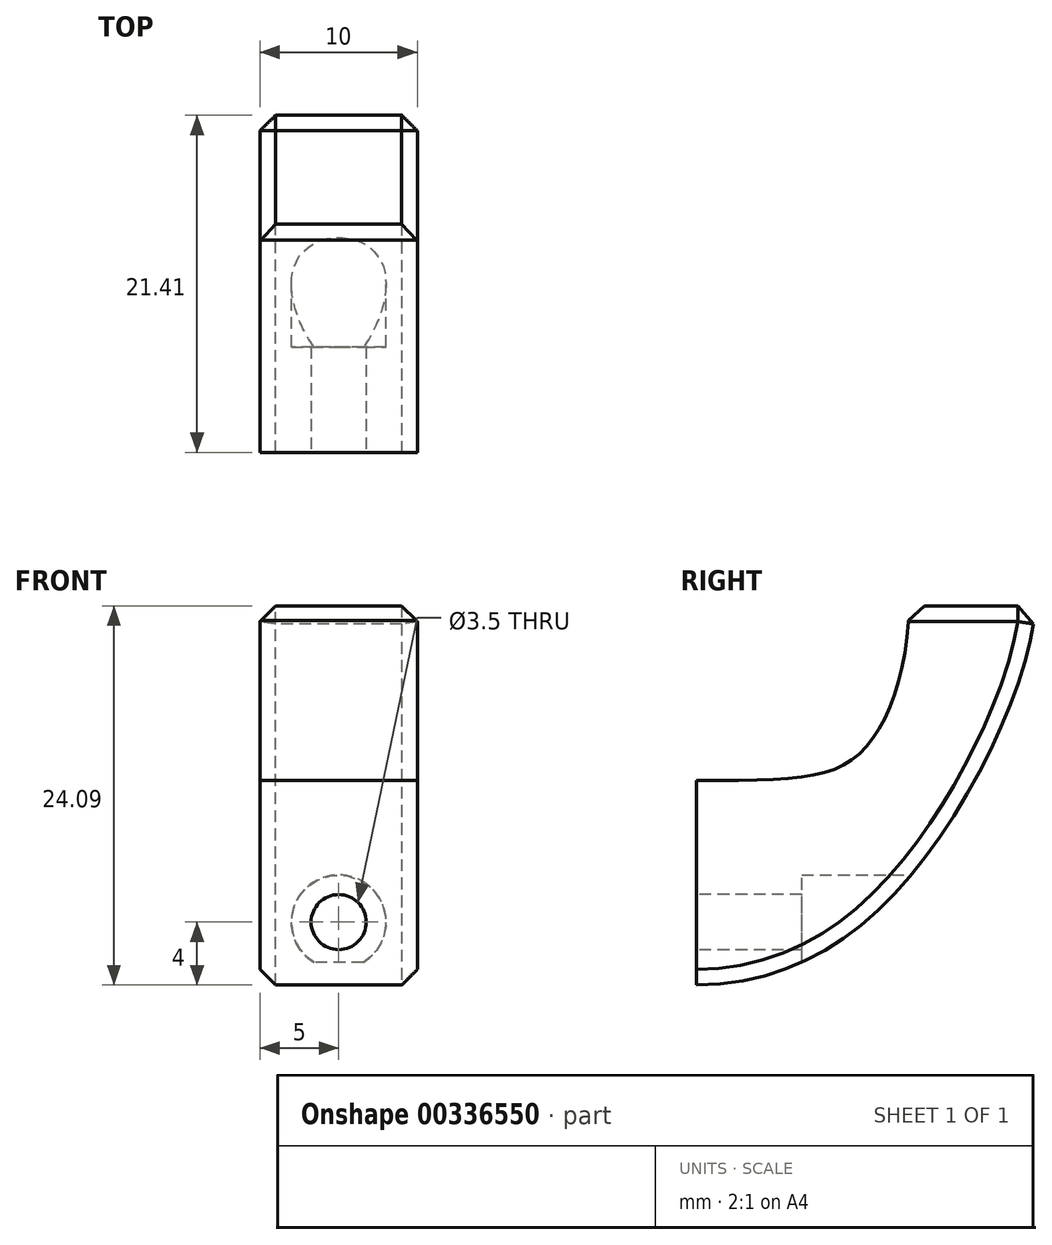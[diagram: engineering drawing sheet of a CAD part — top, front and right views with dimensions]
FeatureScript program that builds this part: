
annotation { "Feature Type Name" : "Feature", "Feature Type Description" : "" }
export const myFeature = defineFeature(function(context is Context, id is Id, definition is map)
    precondition{}
    {
        {
            var Q0;
            Q0=qCreatedBy(makeId("Right.planeOp"),FACE);
            var sketch = newSketch(context, id + "F0", { "sketchPlane" : qUnion([Q0])});
            skLineSegment(sketch, "E0", {"start": v(13.54, 11.1) * mm, "end": v(21.54, 11.1) * mm});
            skFitSpline(sketch, "E1", {"points": [v(0, 0) * mm, v(10.44, 1.78) * mm, v(13.54, 11.1) * mm], "startDerivative": vector(35.3, 0) * mm, "endDerivative": vector(0.9, 25.8) * mm});
            skFitSpline(sketch, "E2", {"points": [v(0, -13) * mm, v(14.33, -5.15) * mm, v(21.54, 11.1) * mm], "startDerivative": vector(37.23, 0.29) * mm, "endDerivative": vector(1.31, 24.38) * mm});
            skLineSegment(sketch, "E3", {"start": v(0, 0) * mm, "end": v(0, -13) * mm});
            skSolve(sketch);
        }
        {
            var Q0;
            Q0 = qSketchRegion(id + "F0", true);
            extrude(context, id + "F1", {"entities" : qUnion([Q0]), "depth" : 10 * mm});
        }
        {
            var Q0;
            Q0=makeQuery(id+"F1.opExtrude","SWEPT_FACE",FACE,{"disambiguationData":[OSD([sQuery(id+"F0.wireOp",EDGE,"E3")])]});
            var sketch = newSketch(context, id + "F2", { "sketchPlane" : qUnion([Q0])});
            skCircle(sketch, "E4", {"center": v(5, -9) * mm, "radius": 1.75 * mm});
            skPoint(sketch, "E4.centerSnap0", {"position": v(5, -13) * mm});
            skSolve(sketch);
        }
        {
            var Q0;
            Q0 = qSketchRegion(id + "F2", true);
            extrude(context, id + "F3", {"entities" : qUnion([Q0]), "operationType" : NewBodyOperationType.REMOVE, "oppositeDirection" : true, "depth" : 25 * mm});
        }
        {
            var Q0;
            Q0=qCreatedBy(makeId("Front.planeOp"),FACE);
            cPlane(context, id + "F4", {"entities" : qUnion([Q0]), "cplaneType" : CPlaneType.OFFSET, "offset" : 25 * mm, "oppositeDirection" : true, "width" : 150 * mm, "height" : 150 * mm});
        }
        {
            var Q0;
            Q0=qCreatedBy(id+"F4.planeOp",FACE);
            var sketch = newSketch(context, id + "F5", { "sketchPlane" : qUnion([Q0])});
            skCircle(sketch, "E5", {"center": v(5, -9) * mm, "radius": 3 * mm});
            skSolve(sketch);
        }
        {
            var Q0;
            Q0 = qSketchRegion(id + "F5", true);
            extrude(context, id + "F6", {"entities" : qUnion([Q0]), "operationType" : NewBodyOperationType.REMOVE, "depth" : 18.3 * mm});
        }
        {
            var Q0;
            Q0=makeQuery(id+"F1.opExtrude","CAP_EDGE",EDGE,{"disambiguationData":[OSD([sQuery(id+"F0.wireOp",EDGE,"E2")])],"isStart":true});
            var Q1;
            Q1=makeQuery(id+"F1.opExtrude","CAP_EDGE",EDGE,{"disambiguationData":[OSD([sQuery(id+"F0.wireOp",EDGE,"E2")])],"isStart":false});
            var Q2;
            Q2=makeQuery(id+"F1.opExtrude","CAP_EDGE",EDGE,{"disambiguationData":[OSD([sQuery(id+"F0.wireOp",EDGE,"E0")])],"isStart":true});
            var Q3;
            Q3=makeQuery(id+"F1.opExtrude","CAP_EDGE",EDGE,{"disambiguationData":[OSD([sQuery(id+"F0.wireOp",EDGE,"E0")])],"isStart":false});
            var Q4;
            Q4=makeQuery(id+"F1.opExtrude","SWEPT_EDGE",EDGE,{"disambiguationData":[OSD([sQuery(id+"F0.wireOp",EDGE,"E0"),sQuery(id+"F0.wireOp",EDGE,"E1")])]});
            var Q5;
            Q5=makeQuery(id+"F1.opExtrude","SWEPT_EDGE",EDGE,{"disambiguationData":[OSD([sQuery(id+"F0.wireOp",EDGE,"E0"),sQuery(id+"F0.wireOp",EDGE,"E2")])]});
            chamfer(context, id + "F7", {"entities" : qUnion([Q0, Q1, Q2, Q3, Q4, Q5]), "width" : 1 * mm, "tangentPropagation" : true});
        }
    });
